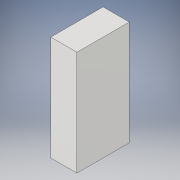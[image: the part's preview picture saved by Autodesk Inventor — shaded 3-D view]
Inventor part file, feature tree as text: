
AUTODESK INVENTOR PART (.ipt)
format: ipt  version: 2017 (Build 210142000, 142)  size: 89,088 bytes
history: native  units: in
note: dims shown in document units (in); Inventor stores cm internally (conversion verified against a paired STEP export)
features: extrude x1, sketch x1
ambient origin geometry x8: Origin, YZ Plane, XZ Plane, XY Plane, X Axis, Y Axis, Z Axis, Center Point
bodies: Solid1 (feature_tree)
feature tree (2):
  extrude  "Extrusion1"  Depth=1.5in
  sketch  "Sketch1"  dims[d0=0.75in d1=1.5in d2=3.0in d3=0.0in]
